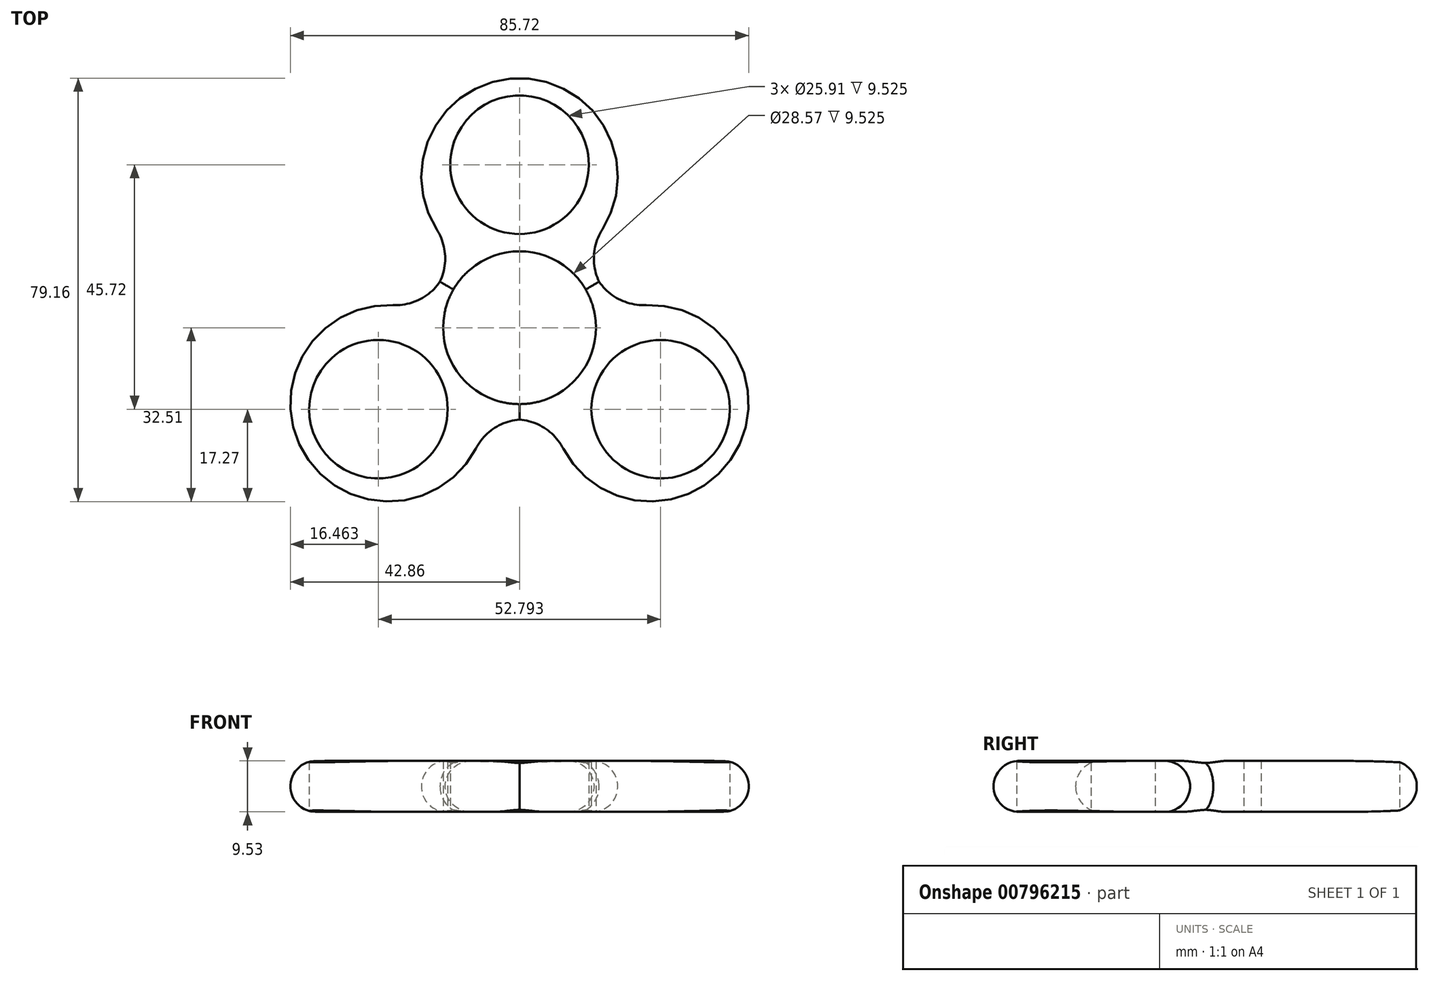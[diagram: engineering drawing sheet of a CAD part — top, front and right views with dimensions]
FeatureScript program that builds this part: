
annotation { "Feature Type Name" : "Feature", "Feature Type Description" : "" }
export const myFeature = defineFeature(function(context is Context, id is Id, definition is map)
    precondition{}
    {
        {
            var Q0;
            Q0=qCreatedBy(makeId("Top.planeOp"),FACE);
            var sketch = newSketch(context, id + "F0", { "sketchPlane" : qUnion([Q0])});
            skCircle(sketch, "E0", {"center": v(0, 0) * mm, "radius": 14.29 * mm});
            skLineSegment(sketch, "E1", {"start": v(0, 0) * mm, "end": v(0, 30.48) * mm});
            skCircle(sketch, "E2", {"center": v(0, 30.48) * mm, "radius": 12.95 * mm});
            skCircle(sketch, "E3.1.0", {"center": v(-26.4, -15.24) * mm, "radius": 12.95 * mm});
            skCircle(sketch, "E3.2.0", {"center": v(26.4, -15.24) * mm, "radius": 12.95 * mm});
            skLineSegment(sketch, "E4", {"start": v(0, 30.48) * mm, "end": v(12.95, 30.48) * mm});
            skLineSegment(sketch, "E5", {"start": v(12.95, 30.48) * mm, "end": v(12.95, 15.24) * mm, "construction": true});
            skLineSegment(sketch, "E6.MirrorCS", {"start": v(-12.95, 30.48) * mm, "end": v(-12.95, 15.24) * mm, "construction": true});
            skPoint(sketch, "E7.visualSharp", {"position": v(12.95, 15.24) * mm});
            skPoint(sketch, "E8.visualSharp", {"position": v(-12.95, 15.24) * mm});
            skLineSegment(sketch, "E9.1.0", {"start": v(-19.92, -26.46) * mm, "end": v(-6.72, -18.84) * mm, "construction": true});
            skLineSegment(sketch, "E9.1.1", {"start": v(-32.87, -4.02) * mm, "end": v(-19.68, 3.6) * mm, "construction": true});
            skLineSegment(sketch, "E9.2.0", {"start": v(32.87, -4.02) * mm, "end": v(19.68, 3.6) * mm, "construction": true});
            skLineSegment(sketch, "E9.2.1", {"start": v(19.92, -26.46) * mm, "end": v(6.72, -18.84) * mm, "construction": true});
            skArc(sketch, "E10", {"start": v(15.5, 18.4) * mm, "mid": v(0, 46.65) * mm, "end": v(-15.5, 18.4) * mm});
            skArc(sketch, "E11.1.0", {"start": v(-23.68, 4.22) * mm, "mid": v(-40.4, -23.32) * mm, "end": v(-8.18, -22.62) * mm});
            skArc(sketch, "E11.2.0", {"start": v(8.18, -22.62) * mm, "mid": v(40.4, -23.32) * mm, "end": v(23.68, 4.22) * mm});
            skArc(sketch, "E12", {"start": v(-14.88, 8.59) * mm, "mid": v(-13.92, 13.57) * mm, "end": v(-15.5, 18.4) * mm});
            skArc(sketch, "E13", {"start": v(-23.68, 4.22) * mm, "mid": v(-18.71, 5.27) * mm, "end": v(-14.88, 8.59) * mm});
            skArc(sketch, "E14.1.0", {"start": v(0, -17.18) * mm, "mid": v(-4.8, -18.84) * mm, "end": v(-8.18, -22.62) * mm});
            skArc(sketch, "E14.1.1", {"start": v(8.18, -22.62) * mm, "mid": v(4.8, -18.84) * mm, "end": v(0, -17.18) * mm});
            skArc(sketch, "E14.2.0", {"start": v(14.88, 8.59) * mm, "mid": v(18.71, 5.27) * mm, "end": v(23.68, 4.22) * mm});
            skArc(sketch, "E14.2.1", {"start": v(15.5, 18.4) * mm, "mid": v(13.92, 13.57) * mm, "end": v(14.88, 8.59) * mm});
            skSolve(sketch);
        }
        {
            var Q0;
            Q0=makeQuery(id+"F0.imprint","IMPRINT",FACE,{"disambiguationData":[TD([[makeQuery(id+"F0.imprint","IMPRINT",EDGE,{"derivedFrom":sQuery(id+"F0.wireOp",EDGE,"E0")}),-1.0]])]});
            extrude(context, id + "F1", {"entities" : qUnion([Q0]), "depth" : 9.52 * mm, "offsetDistance" : 25.4 * mm});
        }
        {
            var Q0;
            Q0=makeQuery(id+"F1.opExtrude","CAP_EDGE",EDGE,{"disambiguationData":[OSD([sQuery(id+"F0.wireOp",EDGE,"E10")])],"isStart":false});
            var Q1;
            Q1=makeQuery(id+"F1.opExtrude","CAP_EDGE",EDGE,{"disambiguationData":[OSD([sQuery(id+"F0.wireOp",EDGE,"E13")])],"isStart":false});
            var Q2;
            Q2=makeQuery(id+"F1.opExtrude","CAP_EDGE",EDGE,{"disambiguationData":[OSD([sQuery(id+"F0.wireOp",EDGE,"E12")])],"isStart":false});
            var Q3;
            Q3=makeQuery(id+"F1.opExtrude","CAP_EDGE",EDGE,{"disambiguationData":[OSD([sQuery(id+"F0.wireOp",EDGE,"E11.1.0")])],"isStart":false});
            var Q4;
            Q4=makeQuery(id+"F1.opExtrude","CAP_EDGE",EDGE,{"disambiguationData":[OSD([sQuery(id+"F0.wireOp",EDGE,"E14.1.1")])],"isStart":false});
            fillet(context, id + "F2", {"entities" : qUnion([Q0, Q1, Q2, Q3, Q4]), "radius" : 4.76 * mm, "tangentPropagation" : true, "allowEdgeOverflow" : false});
        }
        {
            var Q0;
            Q0=makeQuery(id+"F1.opExtrude","CAP_EDGE",EDGE,{"disambiguationData":[OSD([sQuery(id+"F0.wireOp",EDGE,"E10")])],"isStart":true});
            var Q1;
            Q1=makeQuery(id+"F1.opExtrude","CAP_EDGE",EDGE,{"disambiguationData":[OSD([sQuery(id+"F0.wireOp",EDGE,"E12")])],"isStart":true});
            var Q2;
            Q2=makeQuery(id+"F1.opExtrude","CAP_EDGE",EDGE,{"disambiguationData":[OSD([sQuery(id+"F0.wireOp",EDGE,"E11.1.0")])],"isStart":true});
            var Q3;
            Q3=makeQuery(id+"F1.opExtrude","CAP_EDGE",EDGE,{"disambiguationData":[OSD([sQuery(id+"F0.wireOp",EDGE,"E14.1.1")])],"isStart":true});
            fillet(context, id + "F3", {"entities" : qUnion([Q0, Q1, Q2, Q3]), "radius" : 4.76 * mm, "tangentPropagation" : true, "allowEdgeOverflow" : false});
        }
    });
